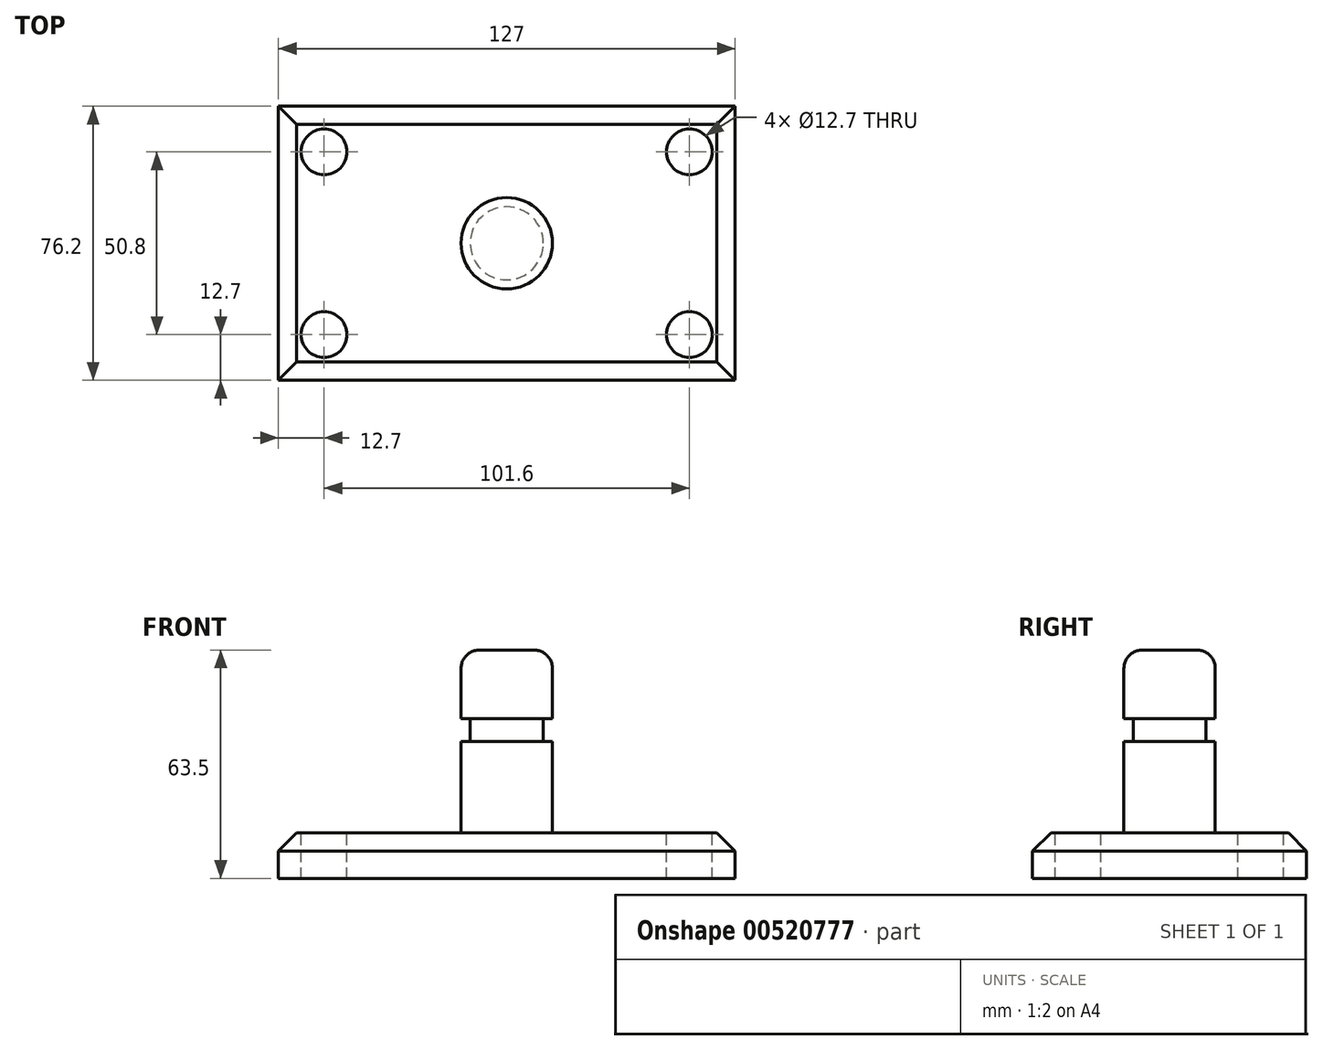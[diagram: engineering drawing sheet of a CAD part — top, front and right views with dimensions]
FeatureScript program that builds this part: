
annotation { "Feature Type Name" : "Feature", "Feature Type Description" : "" }
export const myFeature = defineFeature(function(context is Context, id is Id, definition is map)
    precondition{}
    {
        {
            var Q0;
            Q0=qCreatedBy(makeId("Top.planeOp"),FACE);
            var sketch = newSketch(context, id + "F0", { "sketchPlane" : qUnion([Q0])});
            skLineSegment(sketch, "E0.bottom", {"start": v(-63.5, 38.1) * mm, "end": v(63.5, 38.1) * mm});
            skLineSegment(sketch, "E0.top", {"start": v(-63.5, -38.1) * mm, "end": v(63.5, -38.1) * mm});
            skLineSegment(sketch, "E0.left", {"start": v(-63.5, 38.1) * mm, "end": v(-63.5, -38.1) * mm});
            skLineSegment(sketch, "E0.right", {"start": v(63.5, 38.1) * mm, "end": v(63.5, -38.1) * mm});
            skPoint(sketch, "E0.middle", {"position": v(0, 0) * mm});
            skSolve(sketch);
        }
        {
            var Q0;
            Q0=makeQuery(id+"F0.imprint","IMPRINT",FACE,{"disambiguationData":[TD([[makeQuery(id+"F0.imprint","IMPRINT",EDGE,{"derivedFrom":sQuery(id+"F0.wireOp",EDGE,"E0.bottom")}),-1.0]])]});
            extrude(context, id + "F1", {"entities" : qUnion([Q0]), "depth" : 12.7 * mm, "offsetDistance" : 25.4 * mm});
        }
        {
            var Q0;
            Q0=makeQuery(id+"F1.opExtrude","CAP_FACE",FACE,{"disambiguationData":[OSD([sQuery(id+"F0.wireOp",EDGE,"E0.bottom"),sQuery(id+"F0.wireOp",EDGE,"E0.top"),sQuery(id+"F0.wireOp",EDGE,"E0.left"),sQuery(id+"F0.wireOp",EDGE,"E0.right")])],"isStart":false});
            var sketch = newSketch(context, id + "F2", { "sketchPlane" : qUnion([Q0])});
            skCircle(sketch, "E1", {"center": v(-50.8, 25.4) * mm, "radius": 6.35 * mm});
            skCircle(sketch, "E2", {"center": v(50.8, 25.4) * mm, "radius": 6.35 * mm});
            skCircle(sketch, "E3", {"center": v(50.8, -25.4) * mm, "radius": 6.35 * mm});
            skCircle(sketch, "E4", {"center": v(-50.8, -25.4) * mm, "radius": 6.35 * mm});
            skSolve(sketch);
        }
        {
            var Q0;
            Q0 = qSketchRegion(id + "F2", true);
            extrude(context, id + "F3", {"entities" : qUnion([Q0]), "operationType" : NewBodyOperationType.REMOVE, "endBound" : BoundingType.THROUGH_ALL, "oppositeDirection" : true, "depth" : 25.4 * mm, "offsetDistance" : 25.4 * mm});
        }
        {
            var Q0;
            Q0=qCreatedBy(makeId("Front.planeOp"),FACE);
            var sketch = newSketch(context, id + "F4", { "sketchPlane" : qUnion([Q0])});
            skLineSegment(sketch, "E5.bottom", {"start": v(0, 12.7) * mm, "end": v(12.7, 12.7) * mm});
            skLineSegment(sketch, "E5.top", {"start": v(0, 63.5) * mm, "end": v(12.7, 63.5) * mm});
            skLineSegment(sketch, "E5.left", {"start": v(0, 12.7) * mm, "end": v(0, 63.5) * mm});
            skLineSegment(sketch, "E5.right", {"start": v(12.7, 12.7) * mm, "end": v(12.7, 63.5) * mm});
            skSolve(sketch);
        }
        {
            var Q0;
            Q0 = qSketchRegion(id + "F4", true);
            var Q1;
            Q1=sQuery(id+"F4.wireOp",EDGE,"E5.left");
            revolve(context, id + "F5", {"operationType" : NewBodyOperationType.ADD, "entities" : qUnion([Q0]), "axis" : qUnion([Q1]), "revolveType" : RevolveType.FULL});
        }
        {
            var Q0;
            Q0=qCreatedBy(makeId("Front.planeOp"),FACE);
            var sketch = newSketch(context, id + "F6", { "sketchPlane" : qUnion([Q0])});
            skLineSegment(sketch, "E6.bottom", {"start": v(21.83, 44.45) * mm, "end": v(10.16, 44.45) * mm});
            skLineSegment(sketch, "E6.top", {"start": v(21.83, 38.1) * mm, "end": v(10.16, 38.1) * mm});
            skLineSegment(sketch, "E6.left", {"start": v(21.83, 44.45) * mm, "end": v(21.83, 38.1) * mm});
            skLineSegment(sketch, "E6.right", {"start": v(10.16, 44.45) * mm, "end": v(10.16, 38.1) * mm});
            skSolve(sketch);
        }
        {
            var Q0;
            Q0=makeQuery(id+"F6.imprint","IMPRINT",FACE,{"disambiguationData":[TD([[makeQuery(id+"F6.imprint","IMPRINT",EDGE,{"derivedFrom":sQuery(id+"F6.wireOp",EDGE,"E6.bottom")}),1.0]])]});
            var Q1;
            Q1=makeQuery(id+"F5.opRevolve","SWEPT_FACE",FACE,{"disambiguationData":[OSD([sQuery(id+"F4.wireOp",EDGE,"E5.right")])]});
            revolve(context, id + "F7", {"operationType" : NewBodyOperationType.REMOVE, "entities" : qUnion([Q0]), "axis" : qUnion([Q1]), "revolveType" : RevolveType.FULL, "oppositeDirection" : true});
        }
        {
            var Q0;
            Q0=makeQuery(id+"F5.opRevolve","SWEPT_EDGE",EDGE,{"disambiguationData":[OSD([sQuery(id+"F4.wireOp",EDGE,"E5.top"),sQuery(id+"F4.wireOp",EDGE,"E5.right")])]});
            var Q1;
            Q1=makeQuery(id+"F5.opRevolve","SWEPT_EDGE",EDGE,{"disambiguationData":[OSD([sQuery(id+"F4.wireOp",EDGE,"E5.bottom"),sQuery(id+"F4.wireOp",EDGE,"E5.right")])]});
            fillet(context, id + "F8", {"entities" : qUnion([Q0, Q1]), "radius" : 5.08 * mm, "tangentPropagation" : true, "allowEdgeOverflow" : false});
        }
        {
            var Q0;
            Q0=makeQuery(id+"F1.opExtrude","CAP_EDGE",EDGE,{"disambiguationData":[OSD([sQuery(id+"F0.wireOp",EDGE,"E0.top")])],"isStart":false});
            var Q1;
            Q1=makeQuery(id+"F1.opExtrude","CAP_EDGE",EDGE,{"disambiguationData":[OSD([sQuery(id+"F0.wireOp",EDGE,"E0.left")])],"isStart":false});
            var Q2;
            Q2=makeQuery(id+"F1.opExtrude","CAP_EDGE",EDGE,{"disambiguationData":[OSD([sQuery(id+"F0.wireOp",EDGE,"E0.bottom")])],"isStart":false});
            var Q3;
            Q3=makeQuery(id+"F1.opExtrude","CAP_EDGE",EDGE,{"disambiguationData":[OSD([sQuery(id+"F0.wireOp",EDGE,"E0.right")])],"isStart":false});
            chamfer(context, id + "F9", {"entities" : qUnion([Q0, Q1, Q2, Q3]), "width" : 5.08 * mm, "tangentPropagation" : true});
        }
    });
